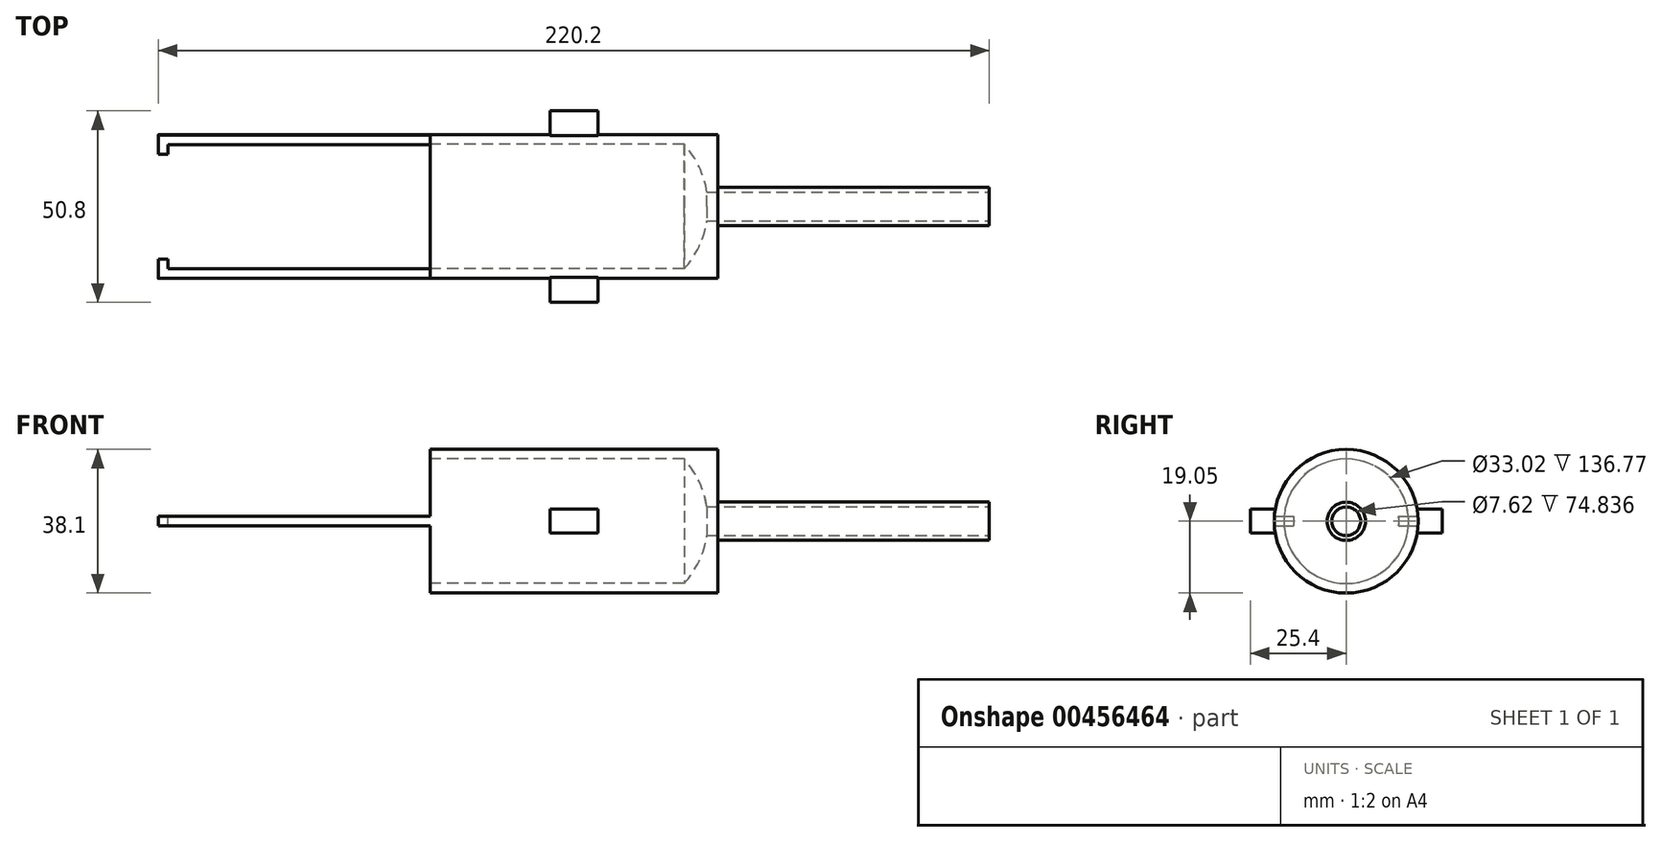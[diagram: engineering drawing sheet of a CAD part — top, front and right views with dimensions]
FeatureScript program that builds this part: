
annotation { "Feature Type Name" : "Feature", "Feature Type Description" : "" }
export const myFeature = defineFeature(function(context is Context, id is Id, definition is map)
    precondition{}
    {
        {
            var Q0;
            Q0=qCreatedBy(makeId("Right.planeOp"),FACE);
            var sketch = newSketch(context, id + "F0", { "sketchPlane" : qUnion([Q0])});
            skCircle(sketch, "E0", {"center": v(0, 0) * mm, "radius": 19.05 * mm});
            skSolve(sketch);
        }
        {
            var Q0;
            Q0=makeQuery(id+"F0.imprint","IMPRINT",FACE,{"disambiguationData":[TD([[makeQuery(id+"F0.imprint","IMPRINT",EDGE,{"derivedFrom":sQuery(id+"F0.wireOp",EDGE,"E0")}),1.0]])]});
            extrude(context, id + "F1", {"entities" : qUnion([Q0]), "oppositeDirection" : true, "depth" : 76.2 * mm + 72 * mm});
        }
        {
            var Q0;
            Q0=qCreatedBy(makeId("Front.planeOp"),FACE);
            var sketch = newSketch(context, id + "F2", { "sketchPlane" : qUnion([Q0])});
            skLineSegment(sketch, "E1", {"start": v(0, 0) * mm, "end": v(-2.54, 0) * mm});
            skLineSegment(sketch, "E2", {"start": v(-2.54, 0) * mm, "end": v(-8.9, 0) * mm});
            skLineSegment(sketch, "E3", {"start": v(-8.9, 0) * mm, "end": v(-148.2, 0) * mm});
            skLineSegment(sketch, "E4", {"start": v(-8.9, 0) * mm, "end": v(-8.9, -16.51) * mm});
            skLineSegment(sketch, "E5", {"start": v(-8.89, -16.51) * mm, "end": v(-76.2, -16.51) * mm});
            skLineSegment(sketch, "E6", {"start": v(-148.2, -16.51) * mm, "end": v(-148.2, 0) * mm});
            skArc(sketch, "E7", {"start": v(-8.89, -16.51) * mm, "mid": v(-4.18, -8.84) * mm, "end": v(-2.54, 0) * mm});
            skPoint(sketch, "E8", {"position": v(-76.2, -16.51) * mm});
            skLineSegment(sketch, "E9", {"start": v(-76.2, -16.51) * mm, "end": v(-145.66, -16.51) * mm});
            skPoint(sketch, "E10.start.orphan", {"position": v(-152.38, -16.51) * mm});
            skLineSegment(sketch, "E11", {"start": v(-145.66, -16.51) * mm, "end": v(-145.66, -13.97) * mm});
            skLineSegment(sketch, "E12", {"start": v(-145.66, -13.97) * mm, "end": v(-148.2, -13.97) * mm});
            skSolve(sketch);
        }
        {
            var Q0;
            Q0=qCreatedBy(makeId("Front.planeOp"),FACE);
            var sketch = newSketch(context, id + "F3", { "sketchPlane" : qUnion([Q0])});
            skLineSegment(sketch, "E13", {"start": v(-31.75, 0) * mm, "end": v(-44.45, 0) * mm});
            skLineSegment(sketch, "E14", {"start": v(-44.45, 0) * mm, "end": v(-44.45, 3.17) * mm});
            skLineSegment(sketch, "E15", {"start": v(-44.45, 3.17) * mm, "end": v(-31.75, 3.18) * mm});
            skLineSegment(sketch, "E16", {"start": v(-31.75, 3.18) * mm, "end": v(-31.75, 0) * mm});
            skLineSegment(sketch, "E17", {"start": v(-31.75, -3.17) * mm, "end": v(-44.45, -3.18) * mm});
            skLineSegment(sketch, "E18", {"start": v(-44.45, -3.18) * mm, "end": v(-44.45, 0) * mm});
            skLineSegment(sketch, "E19", {"start": v(-31.75, -3.17) * mm, "end": v(-31.75, 0) * mm});
            skSolve(sketch);
        }
        {
            var Q0;
            Q0 = qSketchRegion(id + "F3", true);
            extrude(context, id + "F4", {"entities" : qUnion([Q0]), "operationType" : NewBodyOperationType.ADD, "endBound" : BoundingType.SYMMETRIC, "oppositeDirection" : true, "depth" : 50.8 * mm});
        }
        {
            var Q0;
            Q0=qSketchRegion(id+"F2",true);
            var Q1;
            Q1=sQuery(id+"F2.wireOp",EDGE,"E3");
            revolve(context, id + "F5", {"operationType" : NewBodyOperationType.REMOVE, "entities" : qUnion([Q0]), "axis" : qUnion([Q1]), "revolveType" : RevolveType.FULL, "oppositeDirection" : true});
        }
        {
            var Q0;
            Q0=qCreatedBy(makeId("Front.planeOp"),FACE);
            var sketch = newSketch(context, id + "F6", { "sketchPlane" : qUnion([Q0])});
            skLineSegment(sketch, "E20", {"start": v(0, 0) * mm, "end": v(-177.8, 0) * mm});
            skLineSegment(sketch, "E21", {"start": v(-76.2, 0) * mm, "end": v(-76.2, 1.27) * mm});
            skLineSegment(sketch, "E22", {"start": v(-76.2, 1.27) * mm, "end": v(-177.8, 1.27) * mm});
            skLineSegment(sketch, "E23", {"start": v(-177.8, 1.27) * mm, "end": v(-177.8, 0) * mm});
            skLineSegment(sketch, "E24", {"start": v(-76.2, 0) * mm, "end": v(-76.2, -1.27) * mm});
            skLineSegment(sketch, "E25", {"start": v(-76.2, -1.27) * mm, "end": v(-177.8, -1.27) * mm});
            skLineSegment(sketch, "E26", {"start": v(-177.8, -1.27) * mm, "end": v(-177.8, 0) * mm});
            skLineSegment(sketch, "E27", {"start": v(-76.2, 1.27) * mm, "end": v(-76.2, 26.05) * mm});
            skLineSegment(sketch, "E28", {"start": v(-76.2, 26.05) * mm, "end": v(-179, 26.05) * mm});
            skLineSegment(sketch, "E29", {"start": v(-179, 26.05) * mm, "end": v(-177.8, 1.27) * mm});
            skLineSegment(sketch, "E30", {"start": v(-177.8, -1.27) * mm, "end": v(-177.8, -33.07) * mm});
            skLineSegment(sketch, "E31", {"start": v(-177.8, -33.07) * mm, "end": v(-76.2, -33.07) * mm});
            skLineSegment(sketch, "E32", {"start": v(-76.2, -33.07) * mm, "end": v(-76.2, -1.27) * mm});
            skSolve(sketch);
        }
        {
            var Q0;
            Q0=makeQuery(id+"F6.imprint","IMPRINT",FACE,{"disambiguationData":[TD([[makeQuery(id+"F6.imprint","IMPRINT",EDGE,{"derivedFrom":sQuery(id+"F6.wireOp",EDGE,"E22")}),-1.0]])]});
            var Q1;
            Q1=makeQuery(id+"F6.imprint","IMPRINT",FACE,{"disambiguationData":[TD([[makeQuery(id+"F6.imprint","IMPRINT",EDGE,{"derivedFrom":sQuery(id+"F6.wireOp",EDGE,"E25")}),1.0]])]});
            extrude(context, id + "F7", {"entities" : qUnion([Q0, Q1]), "operationType" : NewBodyOperationType.REMOVE, "endBound" : BoundingType.SYMMETRIC, "depth" : 50.8 * mm});
        }
        {
            var Q0;
            Q0=makeQuery(id+"F1.opExtrude","CAP_FACE",FACE,{"disambiguationData":[OSD([sQuery(id+"F0.wireOp",EDGE,"E0")])],"isStart":true});
            var sketch = newSketch(context, id + "F8", { "sketchPlane" : qUnion([Q0])});
            skCircle(sketch, "E33", {"center": v(0, 0) * mm, "radius": 5.08 * mm});
            skSolve(sketch);
        }
        {
            var Q0;
            Q0=makeQuery(id+"F8.imprint","IMPRINT",FACE,{"disambiguationData":[TD([[makeQuery(id+"F8.imprint","IMPRINT",EDGE,{"derivedFrom":sQuery(id+"F8.wireOp",EDGE,"E33")}),1.0]])]});
            extrude(context, id + "F9", {"entities" : qUnion([Q0]), "operationType" : NewBodyOperationType.ADD, "depth" : 72 * mm});
        }
        {
            var Q0;
            Q0=makeQuery(id+"F9.opExtrude","CAP_FACE",FACE,{"disambiguationData":[OSD([sQuery(id+"F8.wireOp",EDGE,"E33")])],"isStart":false});
            var sketch = newSketch(context, id + "F10", { "sketchPlane" : qUnion([Q0])});
            skCircle(sketch, "E34", {"center": v(0, 0) * mm, "radius": 3.81 * mm});
            skSolve(sketch);
        }
        {
            var Q0;
            Q0=makeQuery(id+"F10.imprint","IMPRINT",FACE,{"disambiguationData":[TD([[makeQuery(id+"F10.imprint","IMPRINT",EDGE,{"derivedFrom":sQuery(id+"F10.wireOp",EDGE,"E34")}),1.0]])]});
            extrude(context, id + "F11", {"entities" : qUnion([Q0]), "operationType" : NewBodyOperationType.REMOVE, "oppositeDirection" : true, "depth" : 152.4 * mm});
        }
    });
